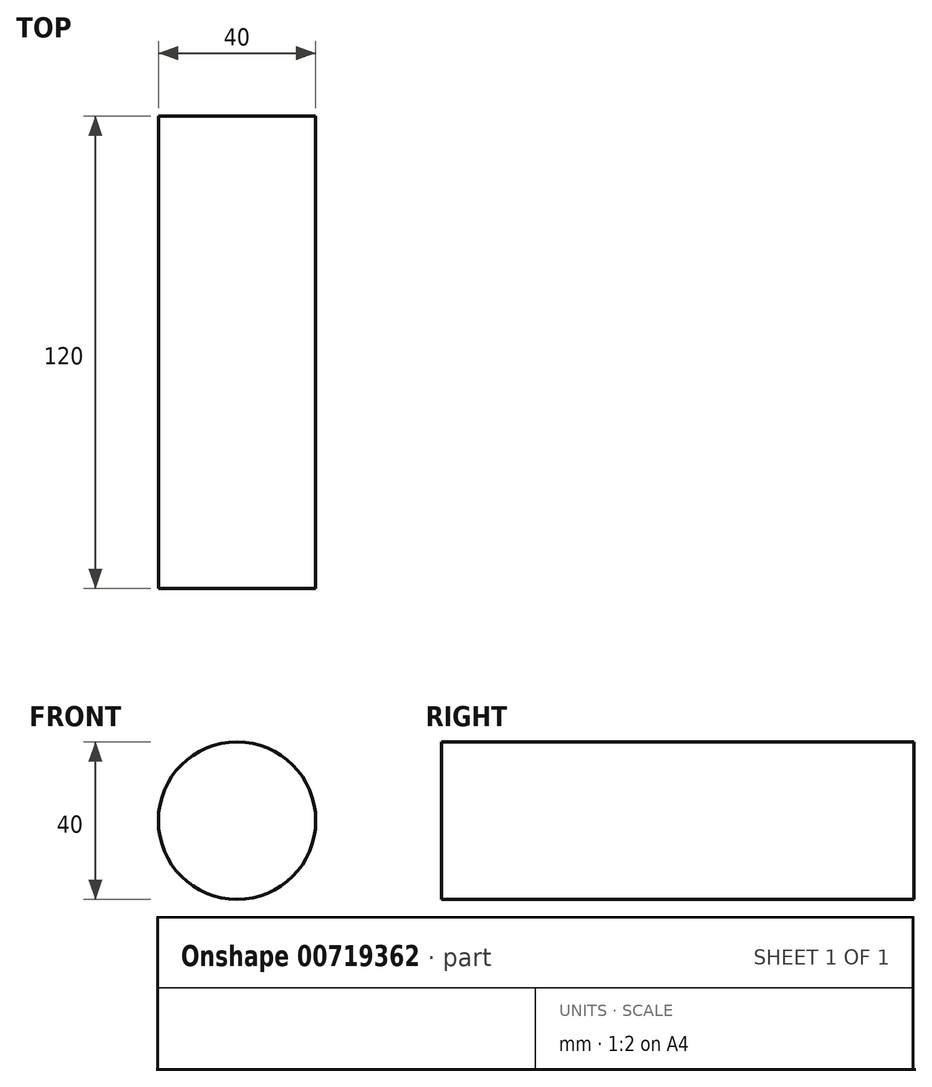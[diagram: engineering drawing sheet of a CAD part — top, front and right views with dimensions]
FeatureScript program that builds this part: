
annotation { "Feature Type Name" : "Feature", "Feature Type Description" : "" }
export const myFeature = defineFeature(function(context is Context, id is Id, definition is map)
    precondition{}
    {
        {
            var Q0;
            Q0=qCreatedBy(makeId("Front.planeOp"),FACE);
            var sketch = newSketch(context, id + "F0", { "sketchPlane" : qUnion([Q0])});
            skCircle(sketch, "E0", {"center": v(0, 0) * mm, "radius": 20 * mm});
            skSolve(sketch);
        }
        {
            var Q0;
            Q0 = qSketchRegion(id + "F0", true);
            extrude(context, id + "F1", {"entities" : qUnion([Q0]), "depth" : 120 * mm, "offsetDistance" : 25 * mm});
        }
    });
